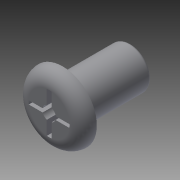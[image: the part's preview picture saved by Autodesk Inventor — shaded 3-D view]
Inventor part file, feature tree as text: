
AUTODESK INVENTOR PART (.ipt)
format: ipt  version: 2015 SP2 (Build 190223200, 223)  size: 149,504 bytes
history: native  units: mm
features: extrude x4, sketch x4, fillet x2
ambient origin geometry x8: Origin, YZ Plane, XZ Plane, XY Plane, X Axis, Y Axis, Z Axis, Center Point
bodies: Solid1 (feature_tree)
feature tree (10):
  extrude  "Extrusion1"  Depth=5.0mm
  extrude  "Extrusion2"  Depth=1.0mm
  extrude  "Extrusion4"  Depth=1.0mm TaperAngle=0.0deg
  fillet  "Fillet1"  Radius=1.0mm
  fillet  "Fillet2"  Radius=1.0mm
  extrude  "Extrusion5"  Depth=0.1mm TaperAngle=0.0deg
  sketch  "Sketch1"  dims[d0=5.0mm d1=3.0mm]
  sketch  "Sketch2"  dims[d2=1.0mm d3=0.0mm d4=3.0mm]
  sketch  "Sketch4"  dims[d5=5.0mm d6=0.0mm d7=1.0mm d8=0.0mm d11=1.0mm d12=0.0mm d13=1.0mm]
  sketch  "Sketch5"  dims[d14=0.2mm d15=0.1mm d16=0.0mm]
